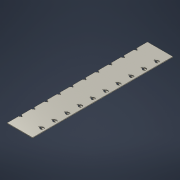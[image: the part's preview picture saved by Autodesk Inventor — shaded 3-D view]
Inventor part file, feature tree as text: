
AUTODESK INVENTOR PART (.ipt)
format: ipt  version: 2022 (Build 260153070, 153G)  size: 592,384 bytes
history: native  units: mm
features: extrude x1, sketch x1, other x1
ambient origin geometry x8: Origin, YZ Plane, XZ Plane, XY Plane, X Axis, Y Axis, Z Axis, Center Point
bodies: Body1 (feature_tree)
feature tree (3):
  extrude  "Выдавливание3"  Depth=145.0mm
  sketch  "Эскиз1"
  other  "Определение1"
